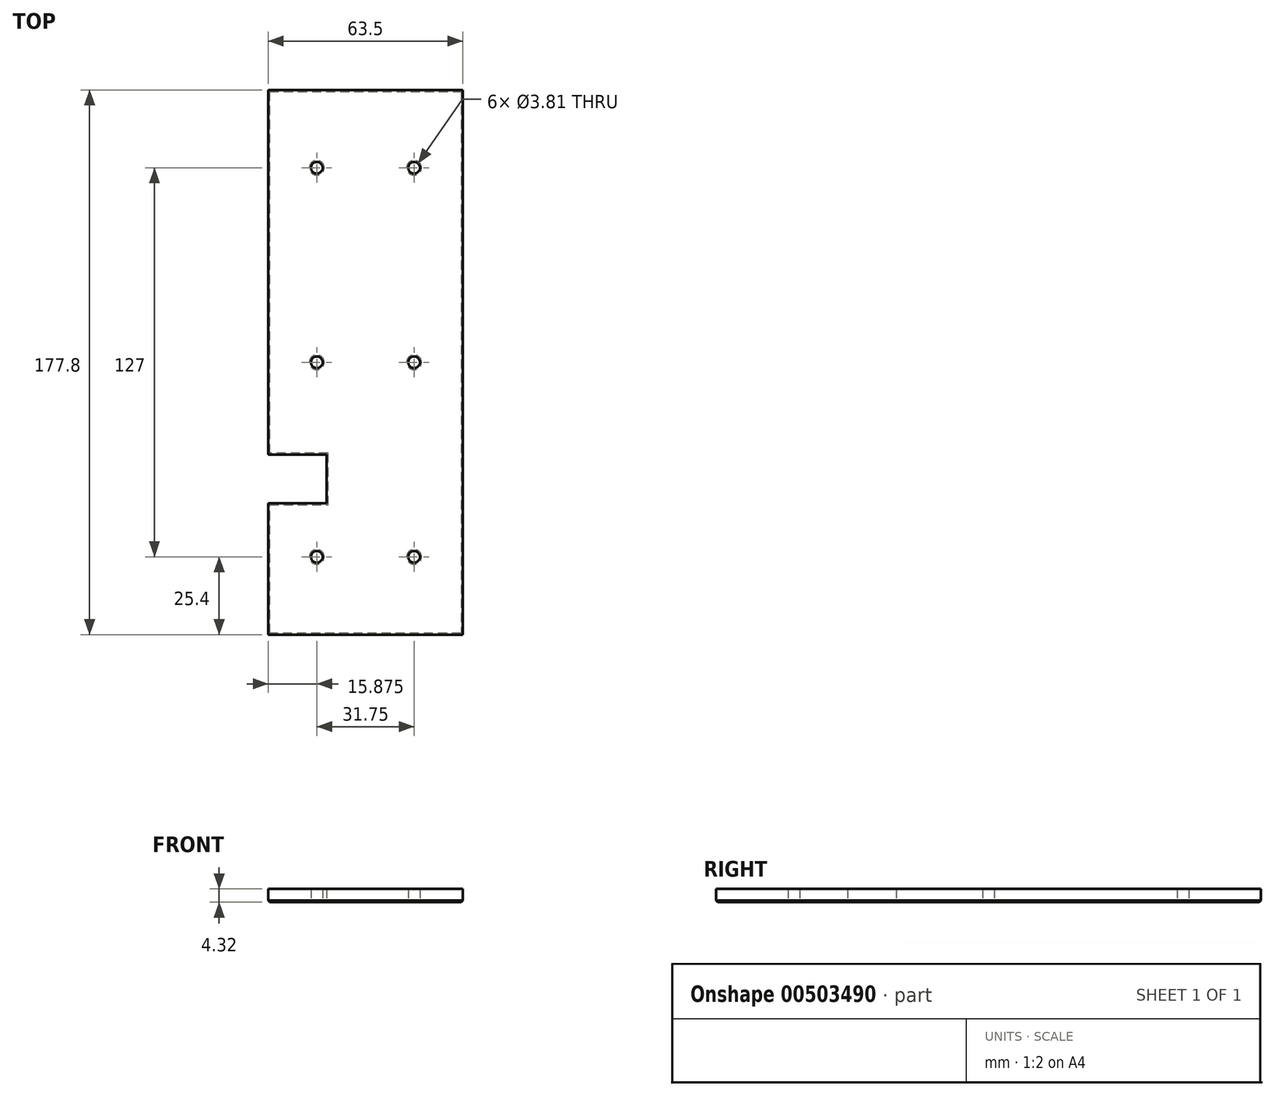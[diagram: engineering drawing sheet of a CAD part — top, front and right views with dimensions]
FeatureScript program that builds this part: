
annotation { "Feature Type Name" : "Feature", "Feature Type Description" : "" }
export const myFeature = defineFeature(function(context is Context, id is Id, definition is map)
    precondition{}
    {
        {
            var Q0;
            Q0=qCreatedBy(makeId("Top.planeOp"),FACE);
            var sketch = newSketch(context, id + "F0", { "sketchPlane" : qUnion([Q0])});
            skLineSegment(sketch, "E0.bottom", {"start": v(31.75, -88.9) * mm, "end": v(-31.75, -88.9) * mm});
            skLineSegment(sketch, "E0.top", {"start": v(31.75, 88.9) * mm, "end": v(-31.75, 88.9) * mm});
            skLineSegment(sketch, "E0.left", {"start": v(31.75, -88.9) * mm, "end": v(31.75, 88.9) * mm});
            skLineSegment(sketch, "E0.right", {"start": v(-31.75, -88.9) * mm, "end": v(-31.75, 88.9) * mm});
            skPoint(sketch, "E0.middle", {"position": v(0, 0) * mm});
            skCircle(sketch, "E1", {"center": v(15.87, 63.5) * mm, "radius": 1.9 * mm});
            skCircle(sketch, "E2", {"center": v(-15.88, 63.5) * mm, "radius": 1.9 * mm});
            skCircle(sketch, "E3", {"center": v(-15.88, 0) * mm, "radius": 1.9 * mm});
            skCircle(sketch, "E4", {"center": v(15.87, 0) * mm, "radius": 1.9 * mm});
            skCircle(sketch, "E5", {"center": v(-15.88, -63.5) * mm, "radius": 1.9 * mm});
            skCircle(sketch, "E6", {"center": v(15.87, -63.5) * mm, "radius": 1.9 * mm});
            skLineSegment(sketch, "E7", {"start": v(-31.75, -46.02) * mm, "end": v(-12.7, -46.02) * mm});
            skLineSegment(sketch, "E8", {"start": v(-12.7, -46.02) * mm, "end": v(-12.7, -30.15) * mm});
            skLineSegment(sketch, "E9", {"start": v(-12.7, -30.15) * mm, "end": v(-31.75, -30.15) * mm});
            skSolve(sketch);
        }
        {
            var Q0;
            {var subQ1=sQuery(id+"F0.wireOp",EDGE,"E0.bottom");Q0=makeQuery(id+"F0.imprint","IMPRINT",FACE,{"disambiguationData":[TD([[makeQuery(id+"F0.imprint","IMPRINT",EDGE,{"derivedFrom":subQ1}),-1.0]])]});}
            extrude(context, id + "F1", {"entities" : qUnion([Q0]), "depth" : 4.32 * mm, "offsetDistance" : 25.4 * mm});
        }
        {
            var Q0;
            Q0=makeQuery(id+"F1.opExtrude","CAP_EDGE",EDGE,{"disambiguationData":[OSD([sQuery(id+"F0.wireOp",EDGE,"E0.bottom")])],"isStart":true});
            var Q1;
            {var subQ0=sQuery(id+"F0.wireOp",EDGE,"E0.right");Q1=makeQuery(id+"F1.opExtrude","CAP_EDGE",EDGE,{"disambiguationData":[OSD([subQ0]),TDD([makeQuery(id+"F0.imprint","IMPRINT",EDGE,{"disambiguationData":[TD([[makeQuery(id+"F0.imprint","INTERSECT",VERTEX,{"derivedFrom":[sQuery(id+"F0.wireOp",EDGE,"E0.bottom"),subQ0]}),-1.0]])],"derivedFrom":subQ0})])],"isStart":true});}
            var Q2;
            Q2=makeQuery(id+"F1.opExtrude","CAP_EDGE",EDGE,{"disambiguationData":[OSD([sQuery(id+"F0.wireOp",EDGE,"E7")])],"isStart":true});
            var Q3;
            Q3=makeQuery(id+"F1.opExtrude","CAP_EDGE",EDGE,{"disambiguationData":[OSD([sQuery(id+"F0.wireOp",EDGE,"E8")])],"isStart":true});
            var Q4;
            Q4=makeQuery(id+"F1.opExtrude","CAP_EDGE",EDGE,{"disambiguationData":[OSD([sQuery(id+"F0.wireOp",EDGE,"E9")])],"isStart":true});
            var Q5;
            {var subQ0=sQuery(id+"F0.wireOp",EDGE,"E0.right");Q5=makeQuery(id+"F1.opExtrude","CAP_EDGE",EDGE,{"disambiguationData":[OSD([subQ0]),TDD([makeQuery(id+"F0.imprint","IMPRINT",EDGE,{"disambiguationData":[TD([[makeQuery(id+"F0.imprint","INTERSECT",VERTEX,{"derivedFrom":[sQuery(id+"F0.wireOp",EDGE,"E0.top"),subQ0]}),1.0]])],"derivedFrom":subQ0})])],"isStart":true});}
            var Q6;
            Q6=makeQuery(id+"F1.opExtrude","CAP_EDGE",EDGE,{"disambiguationData":[OSD([sQuery(id+"F0.wireOp",EDGE,"E0.top")])],"isStart":true});
            var Q7;
            Q7=makeQuery(id+"F1.opExtrude","CAP_EDGE",EDGE,{"disambiguationData":[OSD([sQuery(id+"F0.wireOp",EDGE,"E0.left")])],"isStart":true});
            var Q8;
            Q8=makeQuery(id+"F1.opExtrude","CAP_EDGE",EDGE,{"disambiguationData":[OSD([sQuery(id+"F0.wireOp",EDGE,"E3")])],"isStart":true});
            var Q9;
            Q9=makeQuery(id+"F1.opExtrude","CAP_EDGE",EDGE,{"disambiguationData":[OSD([sQuery(id+"F0.wireOp",EDGE,"E4")])],"isStart":true});
            var Q10;
            Q10=makeQuery(id+"F1.opExtrude","CAP_EDGE",EDGE,{"disambiguationData":[OSD([sQuery(id+"F0.wireOp",EDGE,"E6")])],"isStart":true});
            var Q11;
            Q11=makeQuery(id+"F1.opExtrude","CAP_EDGE",EDGE,{"disambiguationData":[OSD([sQuery(id+"F0.wireOp",EDGE,"E5")])],"isStart":true});
            var Q12;
            Q12=makeQuery(id+"F1.opExtrude","CAP_EDGE",EDGE,{"disambiguationData":[OSD([sQuery(id+"F0.wireOp",EDGE,"E2")])],"isStart":true});
            var Q13;
            Q13=makeQuery(id+"F1.opExtrude","CAP_EDGE",EDGE,{"disambiguationData":[OSD([sQuery(id+"F0.wireOp",EDGE,"E1")])],"isStart":true});
            chamfer(context, id + "F2", {"entities" : qUnion([Q0, Q1, Q2, Q3, Q4, Q5, Q6, Q7, Q8, Q9, Q10, Q11, Q12, Q13]), "width" : 0.5 * mm, "tangentPropagation" : true});
        }
    });
